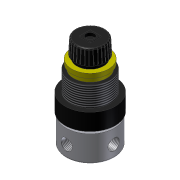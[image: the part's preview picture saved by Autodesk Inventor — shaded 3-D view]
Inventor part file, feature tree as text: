
AUTODESK INVENTOR PART (.ipt)
format: ipt  version: 2013 (Build 170138000, 138)  size: 629,248 bytes
history: native  units: mm (DEFAULTED — no unit token found)
features: extrude x12, sketch x12, projected_geometry x7, fillet x3, pattern_circular x2, thread x2, plane x1
ambient origin geometry x8: Origin, YZ Plane, XZ Plane, XY Plane, X Axis, Y Axis, Z Axis, Center Point
bodies: Solid1 (feature_tree)
feature tree (39):
  extrude  "Extrusion1"  Depth=19.5mm TaperAngle=0.0deg
  extrude  "Extrusion2"  Depth=37.5mm
  extrude  "Extrusion3"  Depth=30.0mm
  extrude  "Extrusion4"  Depth=25.0mm
  extrude  "Extrusion5"  Depth=27.5mm
  extrude  "Extrusion6"  Depth=20.0mm
  extrude  "Extrusion7"  Depth=23.0mm
  extrude  "Extrusion8"  Depth=1.0mm
  fillet  "Fillet1"  Radius=0.5mm
  extrude  "Extrusion9"  Depth=300.0mm TaperAngle=360.0deg
  fillet  "Fillet2"  Radius=10.0mm
  pattern_circular  "Circular Pattern1"  Count=4 Angle=360.0deg
  thread  "Thread1"  [1 undecoded]
  plane  "Work Plane1"
  extrude  "Extrusion10"  Depth=2.0mm TaperAngle=0.0deg
  thread  "Thread2"  [1 undecoded]
  pattern_circular  "Circular Pattern2"  [2 undecoded]
  fillet  "Fillet3"  [1 undecoded]
  extrude  "Extrusion11"  [1 undecoded]
  extrude  "Extrusion12"  [1 undecoded]
  sketch  "Sketch1"  dims[d0=36.0mm d1=19.5mm d2=0.0mm]
  sketch  "Sketch2"  dims[d3=2.0mm d4=0.0mm d5=37.5mm]
  sketch  "Sketch3"  dims[d6=12.5mm d7=0.0mm d8=30.0mm]
  projected_geometry  "Projected Loop1"
  sketch  "Sketch4"  dims[d9=15.0mm d10=0.0mm d11=25.0mm]
  sketch  "Sketch5"  dims[d12=3.3mm d13=0.0mm d14=27.5mm]
  projected_geometry  "Projected Loop2"
  sketch  "Sketch6"  dims[d15=3.3mm d16=0.0mm d17=20.0mm]
  projected_geometry  "Projected Loop3"
  sketch  "Sketch7"  dims[d18=3.0mm d19=0.0mm d20=23.0mm]
  projected_geometry  "Projected Loop4"
  sketch  "Sketch8"  dims[d21=11.0mm d22=-0.523599mm d23=1.0mm d24=0.5mm d25=0.0mm]
  projected_geometry  "Projected Loop5"
  sketch  "Sketch9"  dims[d26=0.15mm d27=300.0mm d29=360.0deg d30=10.0mm d31=0.0mm]
  sketch  "Sketch10"  dims[d32=9.75mm d33=0.0mm]
  projected_geometry  "Projected Loop6"
  sketch  "Sketch11"  dims[d34=10.0mm d35=0.0mm d36=8.5mm d37=40.0mm d39=360.0deg d40=1.0mm]
  sketch  "Sketch12"  dims[d41=6.3mm d42=2.0mm d43=0.0mm d44=0.5mm d45=0.0mm]
  projected_geometry  "Projected Loop7"
note: 7 required parameter values undecoded (feature->parameter linkage not recoverable at this tier; creation-order binding heuristic only, values carry confidence <= 0.55)
